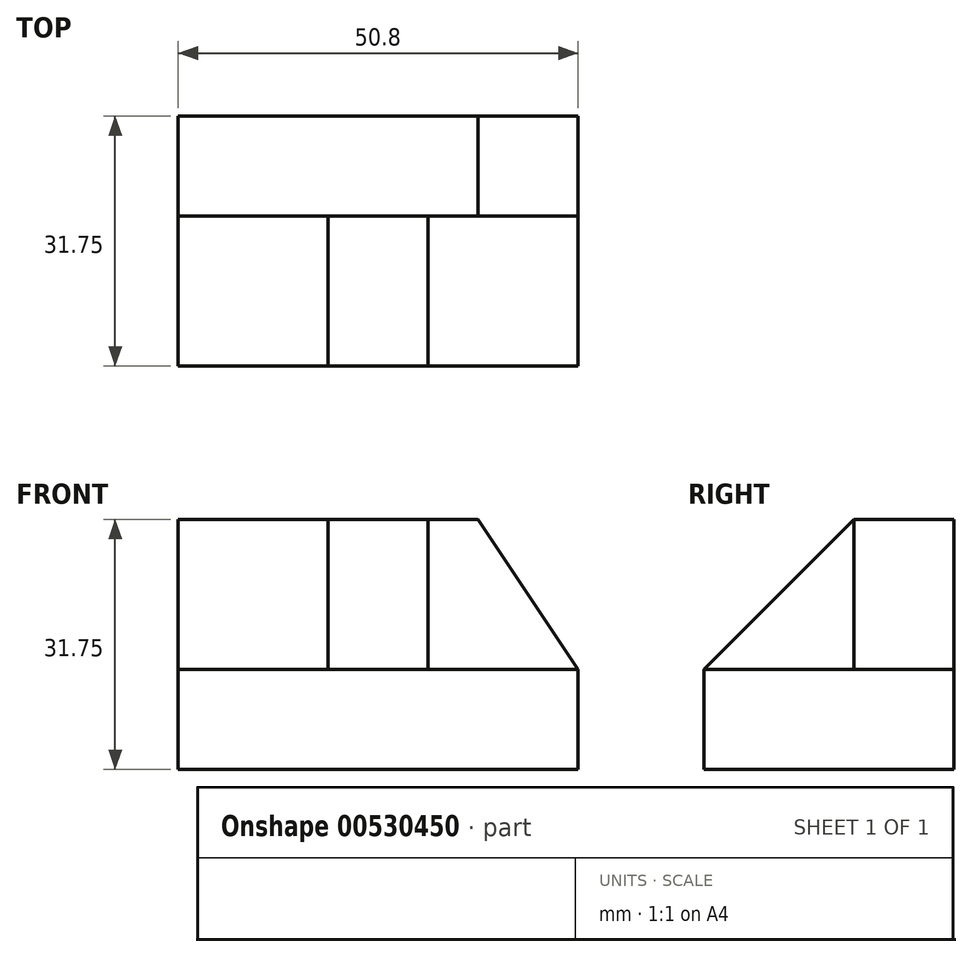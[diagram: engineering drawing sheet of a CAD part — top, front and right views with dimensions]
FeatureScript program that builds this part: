
annotation { "Feature Type Name" : "Feature", "Feature Type Description" : "" }
export const myFeature = defineFeature(function(context is Context, id is Id, definition is map)
    precondition{}
    {
        {
            var Q0;
            Q0=qCreatedBy(makeId("Front.planeOp"),FACE);
            var sketch = newSketch(context, id + "F0", { "sketchPlane" : qUnion([Q0])});
            skLineSegment(sketch, "E0", {"start": v(-61.19, 54.23) * mm, "end": v(-61.19, 22.48) * mm});
            skLineSegment(sketch, "E1", {"start": v(-61.19, 22.48) * mm, "end": v(-10.39, 22.48) * mm});
            skLineSegment(sketch, "E2", {"start": v(-10.39, 22.48) * mm, "end": v(-10.39, 35.18) * mm});
            skLineSegment(sketch, "E3", {"start": v(-10.39, 35.18) * mm, "end": v(-23.09, 54.23) * mm});
            skLineSegment(sketch, "E4", {"start": v(-23.09, 54.23) * mm, "end": v(-61.19, 54.23) * mm});
            skSolve(sketch);
        }
        {
            var Q0;
            Q0=makeQuery(id+"F0.imprint","IMPRINT",FACE,{"disambiguationData":[TD([[makeQuery(id+"F0.imprint","IMPRINT",EDGE,{"derivedFrom":sQuery(id+"F0.wireOp",EDGE,"E0")}),1.0]])]});
            extrude(context, id + "F1", {"entities" : qUnion([Q0]), "depth" : 31.75 * mm, "offsetDistance" : 25.4 * mm});
        }
        {
            var Q0;
            Q0=makeQuery(id+"F1.opExtrude","CAP_FACE",FACE,{"disambiguationData":[OSD([sQuery(id+"F0.wireOp",EDGE,"E0"),sQuery(id+"F0.wireOp",EDGE,"E1"),sQuery(id+"F0.wireOp",EDGE,"E2"),sQuery(id+"F0.wireOp",EDGE,"E3"),sQuery(id+"F0.wireOp",EDGE,"E4")])],"isStart":false});
            var sketch = newSketch(context, id + "F2", { "sketchPlane" : qUnion([Q0])});
            skLineSegment(sketch, "E5", {"start": v(-61.19, 54.23) * mm, "end": v(-42.14, 54.23) * mm});
            skLineSegment(sketch, "E6", {"start": v(-42.14, 54.23) * mm, "end": v(-42.14, 35.18) * mm});
            skLineSegment(sketch, "E7", {"start": v(-42.14, 35.18) * mm, "end": v(-61.19, 35.18) * mm});
            skLineSegment(sketch, "E8", {"start": v(-61.19, 35.18) * mm, "end": v(-61.19, 54.23) * mm});
            skSolve(sketch);
        }
        {
            var Q0;
            Q0=makeQuery(id+"F2.imprint","IMPRINT",FACE,{"disambiguationData":[TD([[makeQuery(id+"F2.imprint","IMPRINT",EDGE,{"derivedFrom":sQuery(id+"F2.wireOp",EDGE,"E5")}),1.0]])]});
            extrude(context, id + "F3", {"entities" : qUnion([Q0]), "operationType" : NewBodyOperationType.REMOVE, "oppositeDirection" : true, "depth" : 19.05 * mm, "offsetDistance" : 25.4 * mm});
        }
        {
            var Q0;
            Q0=makeQuery(id+"F1.opExtrude","CAP_FACE",FACE,{"disambiguationData":[OSD([sQuery(id+"F0.wireOp",EDGE,"E0"),sQuery(id+"F0.wireOp",EDGE,"E1"),sQuery(id+"F0.wireOp",EDGE,"E2"),sQuery(id+"F0.wireOp",EDGE,"E3"),sQuery(id+"F0.wireOp",EDGE,"E4")])],"isStart":false});
            var sketch = newSketch(context, id + "F4", { "sketchPlane" : qUnion([Q0])});
            skLineSegment(sketch, "E9", {"start": v(-10.39, 35.18) * mm, "end": v(-29.44, 35.18) * mm});
            skLineSegment(sketch, "E10", {"start": v(-29.44, 35.18) * mm, "end": v(-29.44, 54.23) * mm});
            skLineSegment(sketch, "E11", {"start": v(-29.44, 54.23) * mm, "end": v(-23.09, 54.23) * mm});
            skLineSegment(sketch, "E12", {"start": v(-23.09, 54.23) * mm, "end": v(-10.39, 35.18) * mm});
            skSolve(sketch);
        }
        {
            var Q0;
            Q0=makeQuery(id+"F4.imprint","IMPRINT",FACE,{"disambiguationData":[TD([[makeQuery(id+"F4.imprint","IMPRINT",EDGE,{"derivedFrom":sQuery(id+"F4.wireOp",EDGE,"E9")}),-1.0]])]});
            extrude(context, id + "F5", {"entities" : qUnion([Q0]), "operationType" : NewBodyOperationType.REMOVE, "oppositeDirection" : true, "depth" : 19.05 * mm, "offsetDistance" : 25.4 * mm});
        }
        {
            var Q0;
            Q0=makeQuery(id+"F5.boolean.opBoolean","COPY",FACE,{"derivedFrom":makeQuery(id+"F5.opExtrude","SWEPT_FACE",FACE,{"disambiguationData":[OSD([sQuery(id+"F4.wireOp",EDGE,"E10")])]})});
            var sketch = newSketch(context, id + "F6", { "sketchPlane" : qUnion([Q0])});
            skLineSegment(sketch, "E13", {"start": v(-12.7, 54.23) * mm, "end": v(-31.75, 35.18) * mm});
            skLineSegment(sketch, "E14", {"start": v(-31.75, 35.18) * mm, "end": v(-31.75, 54.23) * mm});
            skLineSegment(sketch, "E15", {"start": v(-31.75, 54.23) * mm, "end": v(-12.7, 54.23) * mm});
            skSolve(sketch);
        }
        {
            var Q0;
            Q0=makeQuery(id+"F6.imprint","IMPRINT",FACE,{"disambiguationData":[TD([[makeQuery(id+"F6.imprint","IMPRINT",EDGE,{"derivedFrom":sQuery(id+"F6.wireOp",EDGE,"E13")}),-1.0]])]});
            extrude(context, id + "F7", {"entities" : qUnion([Q0]), "operationType" : NewBodyOperationType.REMOVE, "endBound" : BoundingType.THROUGH_ALL, "oppositeDirection" : true, "depth" : 25.4 * mm, "offsetDistance" : 25.4 * mm});
        }
    });
